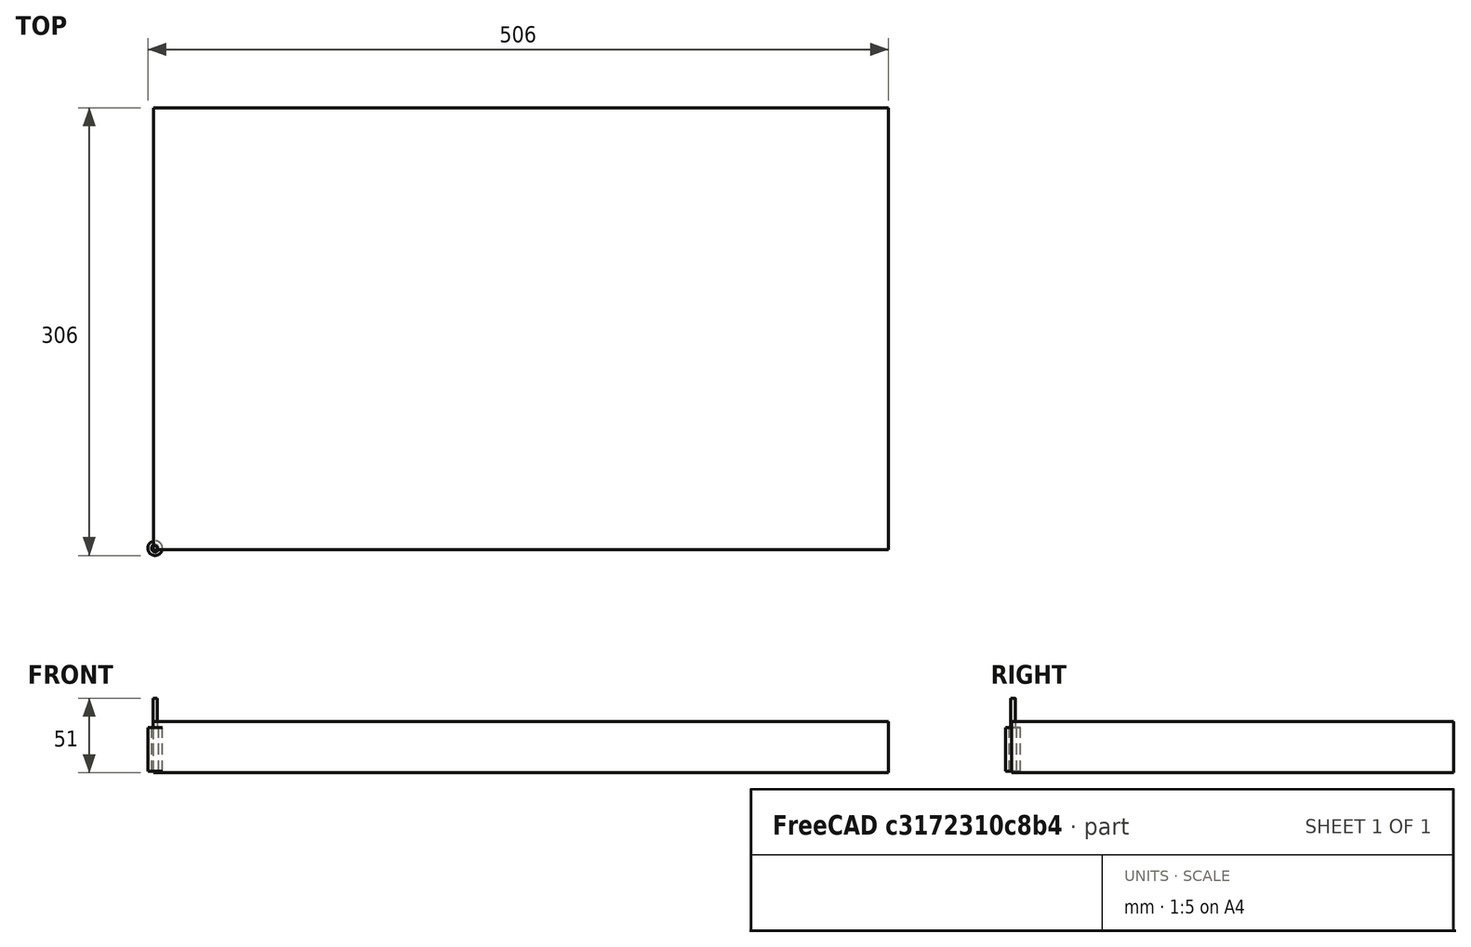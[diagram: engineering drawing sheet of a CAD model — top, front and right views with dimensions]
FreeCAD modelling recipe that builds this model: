
FCSTD DOCUMENT  (FreeCAD 0.19R24212 (Git))
Label: decouverte
License: Creative Commons Attribution
LicenseURL: http://creativecommons.org/licenses/by/4.0/
objects: Path::FeaturePython×6, Part::FeaturePython×5, PartDesign::SubShapeBinder×3, PartDesign::Pad×2, App::DocumentObjectGroup×2, Mesh::FeaturePython×2, Sketcher::SketchObject×1, PartDesign::AdditiveSphere×1, Part::Part2DObjectPython×1, PartDesign::Pocket×1, PartDesign::Body×1, App::FeaturePython×1, Path::FeatureCompoundPython×1
note: 21 computed .brp shape members not serialized (recipe doc carries the construction recipe); baked Part::Feature solids carry a one-line shape summary decoded from their .brp

FEATURE [Sketcher::SketchObject] Sketch
  FullyConstrained = true
  MapMode = 5
  Support = -> [XY_Plane]
  sketch-geometry (4):
    g0: LineSegment StartX=0 StartY=0 StartZ=0 EndX=500 EndY=0 EndZ=0
    g1: LineSegment StartX=500 StartY=0 StartZ=0 EndX=500 EndY=300 EndZ=0
    g2: LineSegment StartX=500 StartY=300 StartZ=0 EndX=0 EndY=300 EndZ=0
    g3: LineSegment StartX=0 StartY=300 StartZ=0 EndX=0 EndY=0 EndZ=0
  constraints (11):
    c: Coincident(g0,g1)
    c: Coincident(g1,g2)
    c: Coincident(g2,g3)
    c: Coincident(g3,g0)
    c: Horizontal(g0)
    c: Horizontal(g2)
    c: Vertical(g1)
    c: Vertical(g3)
    c: Coincident(g0,g-1)
    c: DistanceX(g2,g2) = 500
    c: DistanceY(g1,g1) = 300
FEATURE [PartDesign::Pad] Pad
  Direction = (1,1,1)
  Length = 18
  Length2 = 100
  Profile = -> Sketch
  Refine = true
  Type = 0
FEATURE [PartDesign::AdditiveSphere] Sphere
  Angle1 = 23
  Angle2 = 90
  Angle3 = 360
  AttacherType = Attacher::AttachEngine3D
  AttachmentOffset = pos=(50,50,8) rot=(0,0,1;0rad)
  BaseFeature = -> Pad
  MapMode = 5
  Placement = pos=(50,50,8) rot=(0,0,1;0rad)
  Radius = 25
  Refine = true
  Support = -> [XY_Plane]
FEATURE [Part::Part2DObjectPython] ShapeString  # Draft 2D object (typed FeaturePython)
  FontFile = <path>
  Placement = pos=(63,120,18) rot=(0,0,1;0rad)
  Size = 36
  String = Twitch !
  Tracking = 5
FEATURE [PartDesign::SubShapeBinder] Binder  label="Binder Total"
  BindMode = 0
  ClaimChildren = false
  Context = -> Body [Binder.]
  Fuse = false
  MakeFace = true
  PartialLoad = false
  Relative = true
  Support = -> [ShapeString]
  _Version = 2
FEATURE [PartDesign::SubShapeBinder] Binder001  label="Binder T"
  BindMode = 0
  ClaimChildren = false
  Context = -> Body [Binder001.]
  Fuse = false
  MakeFace = true
  PartialLoad = false
  Relative = true
  Support = -> [ShapeString[Face1,Face4,Face3,Face6,Face8,Face9]]
  _Version = 2
FEATURE [PartDesign::SubShapeBinder] Binder002  label="Binder W"
  BindMode = 0
  ClaimChildren = false
  Context = -> Body [Binder002.]
  Fuse = false
  MakeFace = true
  PartialLoad = false
  Relative = true
  Support = -> [ShapeString[Face2,Face5,Face7]]
  _Version = 2
FEATURE [PartDesign::Pocket] Pocket
  BaseFeature = -> Sphere
  Length = 2
  Length2 = 100
  Placement = pos=(50,50,8) rot=(0,0,1;0rad)
  Profile = -> Binder001
  Refine = true
  Type = 0
FEATURE [PartDesign::Pad] Pad001
  BaseFeature = -> Pocket
  Direction = (1,1,1)
  Length = 2
  Length2 = 100
  Placement = pos=(50,50,8) rot=(0,0,1;0rad)
  Profile = -> Binder002
  Refine = true
  Type = 0
FEATURE [PartDesign::Body] Body
  Group = -> [Sketch,Pad,Sphere,Binder,Binder001,Binder002,Pocket,Pad001]
  Origin = -> Origin
  Tip = -> Pad001
FEATURE [App::FeaturePython] SetupSheet  # Path/CAM operation (typed FeaturePython)
  ClearanceHeightExpression = OpStockZMax+SetupSheet.ClearanceHeightOffset
  ClearanceHeightOffset = 5
  CoolantMode = 0
  CoolantModes = None | Flood | Mist
  FinalDepthExpression = OpFinalDepth
  HorizRapid = 0
  SafeHeightExpression = OpStockZMax+SetupSheet.SafeHeightOffset
  SafeHeightOffset = 3
  StartDepthExpression = OpStartDepth
  StepDownExpression = OpToolDiameter
  VertRapid = 0
FEATURE [Part::FeaturePython] Clone  label="Model-Body"  # Draft clone (typed FeaturePython)
  AttacherType = Attacher::AttachEngine3D
  Fuse = false
  Objects = -> [Body]
  PathResource = Model
  Scale = (1,1,1)
FEATURE [App::DocumentObjectGroup] Model
  Group = -> [Clone]
FEATURE [Part::FeaturePython] ToolBit  label="Endmill"  # Path/CAM toolbit (typed FeaturePython)
  BitPropertyNames = Chipload | CuttingEdgeHeight | Diameter | Flutes | Length | Material | ShankDiameter
  BitShape = <path>
  Chipload = 0
  CuttingEdgeHeight = 30
  Diameter = 5
  Flutes = 0
  Length = 50
  Material = 0
  ShankDiameter = 3
  ShapeName = endmill
FEATURE [Path::FeaturePython] TC__Default_Tool  label="TC: Default Tool"  # Path/CAM operation (typed FeaturePython)
  HorizFeed = 0
  HorizRapid = 0
  SpindleDir = 0
  SpindleSpeed = 0
  Tool = -> ToolBit
  ToolNumber = 1
  VertFeed = 0
  VertRapid = 0
  expr: VertRapid = SetupSheet.VertRapid
  expr: HorizRapid = SetupSheet.HorizRapid
FEATURE [Part::FeaturePython] Stock  # WARN: FeaturePython — macro-defined, semantics opaque (R4)
  Base = -> Model
  ExtXneg = 1
  ExtXpos = 1
  ExtYneg = 1
  ExtYpos = 1
  ExtZneg = 1
  ExtZpos = 1
  StockType = FromBase
FEATURE [Part::FeaturePython] ToolBit001  label="5mm Endmill"  # Path/CAM toolbit (typed FeaturePython)
  BitPropertyNames = Chipload | CuttingEdgeHeight | Diameter | Flutes | Length | Material | ShankDiameter
  BitShape = <path>
  Chipload = 0
  CuttingEdgeHeight = 30
  Diameter = 5
  File = <userpath>/.FreeCAD/Toolbit/Bit/5mm_Endmill.fctb
  Flutes = 0
  Length = 50
  Material = 0
  ShankDiameter = 3
  ShapeName = endmill
FEATURE [Path::FeaturePython] TC__5mm_Endmill  label="TC: 5mm Endmill"  # Path/CAM operation (typed FeaturePython)
  HorizFeed = 0
  HorizRapid = 0
  SpindleDir = 0
  SpindleSpeed = 0
  Tool = -> ToolBit001
  ToolNumber = 1
  VertFeed = 0
  VertRapid = 0
  expr: VertRapid = SetupSheet.VertRapid
  expr: HorizRapid = SetupSheet.HorizRapid
FEATURE [Part::FeaturePython] ToolBit002  label="10mm Endmill001"  # Path/CAM toolbit (typed FeaturePython)
  BitPropertyNames = Chipload | CuttingEdgeHeight | Diameter | Flutes | Length | Material | ShankDiameter
  BitShape = <path>
  Chipload = 0
  CuttingEdgeHeight = 30
  Diameter = 10
  File = <userpath>/.FreeCAD/Toolbit/Bit/5mm_Endmill.fctb
  Flutes = 0
  Length = 50
  Material = 0
  ShankDiameter = 3
  ShapeName = endmill
FEATURE [Path::FeaturePython] TC__10mm_Endmill001  label="TC: 10mm Endmill001"  # Path/CAM operation (typed FeaturePython)
  HorizFeed = 0
  HorizRapid = 0
  SpindleDir = 0
  SpindleSpeed = 0
  Tool = -> ToolBit002
  ToolNumber = 1
  VertFeed = 0
  VertRapid = 0
  expr: VertRapid = SetupSheet.VertRapid
  expr: HorizRapid = SetupSheet.HorizRapid
FEATURE [App::DocumentObjectGroup] Tools
  Group = -> [TC__Default_Tool,TC__5mm_Endmill,TC__10mm_Endmill001]
FEATURE [Path::FeaturePython] Pocket_Shape  # Path/CAM operation (typed FeaturePython)
  Active = true
  AreaParams:
    Tolerance = 1e-07
    FitArcs = True
    Simplify = False
    CleanDistance = 0.0
    Accuracy = 0.01
    Unit = 1.0
    MinArcPoints = 4
    MaxArcPoints = 100
    ClipperScale = 10000000.0
    Fill = 0
    Coplanar = 0
    Reorient = True
    Outline = False
    Explode = False
    OpenMode = 0
    Deflection = 0.01
    SubjectFill = 0
    ClipFill = 0
    Offset = 0.0
    ExtraPass = 0
    Stepover = 0.0
    LastStepover = 0.0
    JoinType = 0
    EndType = 0
    MiterLimit = 2.0
    RoundPrecision = 0.0
    PocketMode = 4
    ToolRadius = 5.0
    PocketExtraOffset = 0.0
    PocketStepover = 10.0
    PocketLastStepover = 0.0
    FromCenter = True
    Angle = 45.0
    AngleShift = 0.0
    Shift = 0.0
    Thicken = False
    SectionCount = -1
    Stepdown = 1.0
    SectionOffset = 0.0
    SectionTolerance = 1e-06
    SectionMode = 2
    Project = False
  AttemptInverseAngle = true
  Base = -> [Clone]
  ClearanceHeight = 39
  CoolantMode = None
  CutMode = 0
  CycleTime = Erreur de temps de cycle
  EnableRotation = 0
  ExtensionCorners = true
  ExtensionLengthDefault = 5
  ExtraOffset = 0
  FinalDepth = 20
  FinishDepth = 0
  InverseAngle = false
  KeepToolDown = false
  LimitDepthToFace = true
  MinTravel = false
  OffsetPattern = 3
  OpFinalDepth = 20
  OpStartDepth = 34
  OpStockZMax = 34
  OpStockZMin = -1
  OpToolDiameter = 10
  PathParams = {'orientation': 1, 'feedrate': 0.0, 'feedrate_v': 0.0, 'verbose': True, 'resume_height': 37.0, 'retraction': 39.0, 'return_end': True, 'preamble': False, 'start': Vector (180.9681972786922, 161.80504771171422, 39.0)}
  ReverseDirection = false
  SafeHeight = 37
  StartAt = 0
  StartDepth = 34
  StartPoint = (0,0,0)
  StepDown = 10
  StepOver = 100
  ToolController = -> TC__10mm_Endmill001
  UseOutline = false
  UseStartPoint = false
  ZigZagAngle = 45
  expr: StartDepth = OpStartDepth
  expr: FinalDepth = OpFinalDepth
  expr: StepDown = OpToolDiameter
  expr: SafeHeight = OpStockZMax + SetupSheet.SafeHeightOffset
  expr: ClearanceHeight = OpStockZMax + SetupSheet.ClearanceHeightOffset
  expr: ExtensionLengthDefault = OpToolDiameter / 2
FEATURE [Mesh::FeaturePython] CutMaterial  # WARN: FeaturePython — macro-defined, semantics opaque (R4)
FEATURE [Mesh::FeaturePython] CutMaterial001  # WARN: FeaturePython — macro-defined, semantics opaque (R4)
FEATURE [Path::FeaturePython] Profile  # Path/CAM operation (typed FeaturePython)
  Active = true
  AreaParams:
    Tolerance = 1e-07
    FitArcs = True
    Simplify = False
    CleanDistance = 0.0
    Accuracy = 0.01
    Unit = 1.0
    MinArcPoints = 4
    MaxArcPoints = 100
    ClipperScale = 10000000.0
    Fill = 0
    Coplanar = 0
    Reorient = True
    Outline = False
    Explode = False
    OpenMode = 0
    Deflection = 0.01
    SubjectFill = 0
    ClipFill = 0
    Offset = 10.0
    ExtraPass = 0
    Stepover = 0.0
    LastStepover = 0.0
    JoinType = 0
    EndType = 0
    MiterLimit = 2.0
    RoundPrecision = 0.0
    PocketMode = 0
    ToolRadius = 1.0
    PocketExtraOffset = 0.0
    PocketStepover = 0.0
    PocketLastStepover = 0.0
    FromCenter = False
    Angle = 45.0
    AngleShift = 0.0
    Shift = 0.0
    Thicken = False
    SectionCount = -1
    Stepdown = 1.0
    SectionOffset = 0.0
    SectionTolerance = 1e-06
    SectionMode = 2
    Project = False
  AttemptInverseAngle = true
  Base = -> [Clone]
  ClearanceHeight = 39
  CoolantMode = None
  CycleTime = Erreur de temps de cycle
  Direction = 0
  EnableRotation = 0
  FinalDepth = 18
  HandleMultipleFeatures = 0
  InverseAngle = false
  JoinType = 0
  LimitDepthToFace = true
  MiterLimit = 0.1
  OffsetExtra = 5
  OpFinalDepth = 18
  OpStartDepth = 34
  OpStockZMax = 34
  OpStockZMin = -1
  OpToolDiameter = 10
  PathParams = {'orientation': 1, 'feedrate': 0.0, 'feedrate_v': 0.0, 'verbose': True, 'resume_height': 37.0, 'retraction': 39.0, 'return_end': True, 'preamble': False}
  ReverseDirection = false
  SafeHeight = 37
  Side = 0
  StartDepth = 34
  StartPoint = (0,0,0)
  StepDown = 10
  ToolController = -> TC__10mm_Endmill001
  UseComp = true
  UseStartPoint = false
  processCircles = false
  processHoles = false
  processPerimeter = true
  expr: StartDepth = OpStartDepth
  expr: FinalDepth = OpFinalDepth
  expr: StepDown = OpToolDiameter
  expr: SafeHeight = OpStockZMax + SetupSheet.SafeHeightOffset
  expr: ClearanceHeight = OpStockZMax + SetupSheet.ClearanceHeightOffset
FEATURE [Path::FeatureCompoundPython] Operations  # Path/CAM operation (typed FeaturePython)
  Group = -> [Profile,Pocket_Shape]
  UsePlacements = false
FEATURE [Path::FeaturePython] Job  # Path/CAM operation (typed FeaturePython)
  CycleTime = 00:00:00
  Fixtures = G54
  GeometryTolerance = 0.01
  Model = -> Model
  Operations = -> Operations
  OrderOutputBy = 0
  PostProcessor = 1
  SetupSheet = -> SetupSheet
  SplitOutput = false
  Stock = -> Stock
  Tools = -> Tools
note: 4 file-system paths scrubbed to <path> (originals preserved in the JSON sidecar)
